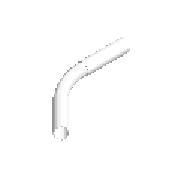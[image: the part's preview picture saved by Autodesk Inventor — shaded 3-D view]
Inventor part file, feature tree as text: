
AUTODESK INVENTOR PART (.ipt)
format: ipt  version: 2023 (Build 270158000, 158)  size: 201,216 bytes
history: native  units: mm (DEFAULTED — no unit token found)
features: other x6, sketch x2, revolve x2, sweep x1
ambient origin geometry x8: Origin, YZ Plane, XZ Plane, XY Plane, X Axis, Y Axis, Z Axis, Center Point
bodies: Solid1 (feature_tree)
feature tree (11):
  sketch  "Sketch1"  dims[d0=182.0mm d1=91.0mm]
  revolve  "Revolve1"  [1 undecoded]
  revolve  "Revolve2"  [1 undecoded]
  sketch  "Sketch2"  dims[d2=103.6mm d3=110.0mm d4=116.4mm d5=203.0mm d6=203.0mm d7=182.0mm d8=91.0mm d9=103.6mm d10=110.0mm d11=116.4mm d36=90.0deg d37=90.0deg d12=45.0deg d13=0.0mm d40=0.0mm]
  sweep  "Sweep1"
  other  "Work Point3"
  other  "Work Point4"
  other  "Work Axis2"
  other  "Work Point5"
  other  "Work Axis3"
  other  "Work Point6"
note: 2 required parameter values undecoded (feature->parameter linkage not recoverable at this tier; creation-order binding heuristic only, values carry confidence <= 0.55)
